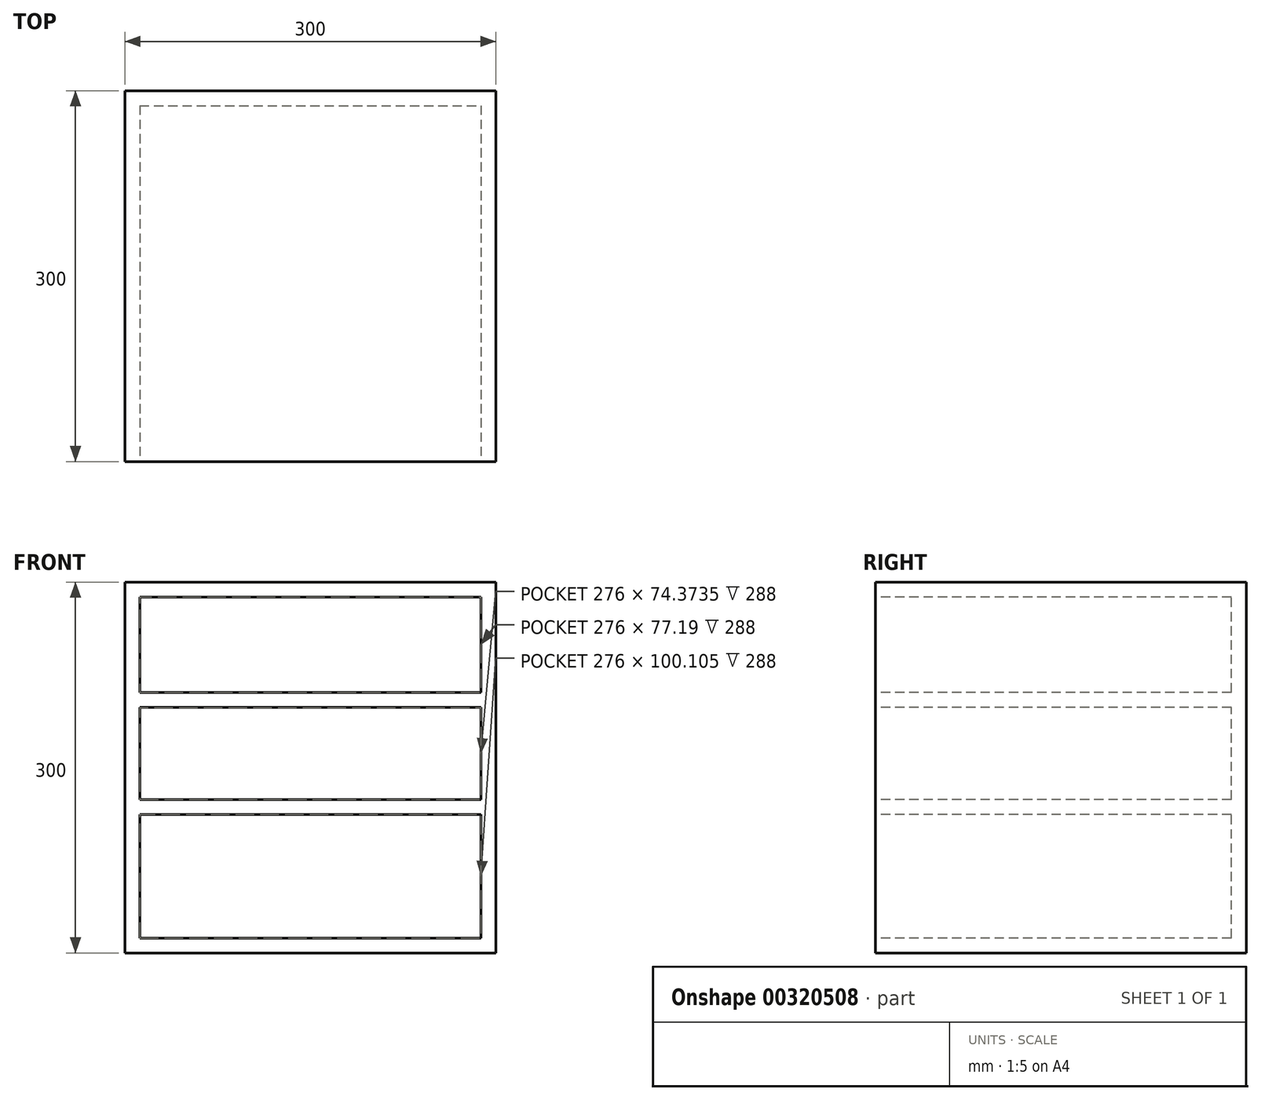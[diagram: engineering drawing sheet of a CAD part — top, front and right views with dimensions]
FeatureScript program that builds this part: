
annotation { "Feature Type Name" : "Feature", "Feature Type Description" : "" }
export const myFeature = defineFeature(function(context is Context, id is Id, definition is map)
    precondition{}
    {
        {
            var Q0;
            Q0=qCreatedBy(makeId("Front.planeOp"),FACE);
            var sketch = newSketch(context, id + "F0", { "sketchPlane" : qUnion([Q0])});
            skLineSegment(sketch, "E0.bottom", {"start": v(-150, -150) * mm, "end": v(150, -150) * mm});
            skLineSegment(sketch, "E0.top", {"start": v(-150, 150) * mm, "end": v(150, 150) * mm});
            skLineSegment(sketch, "E0.left", {"start": v(-150, -150) * mm, "end": v(-150, 150) * mm});
            skLineSegment(sketch, "E0.right", {"start": v(150, -150) * mm, "end": v(150, 150) * mm});
            skPoint(sketch, "E0.middle", {"position": v(0, 0) * mm});
            skSolve(sketch);
        }
        {
            var Q0;
            Q0=makeQuery(id+"F0.imprint","IMPRINT",FACE,{"disambiguationData":[TD([[makeQuery(id+"F0.imprint","IMPRINT",EDGE,{"derivedFrom":sQuery(id+"F0.wireOp",EDGE,"E0.bottom")}),1.0]])]});
            extrude(context, id + "F1", {"entities" : qUnion([Q0]), "oppositeDirection" : true, "depth" : 300 * mm});
        }
        {
            var Q0;
            Q0=makeQuery(id+"F1.opExtrude","CAP_FACE",FACE,{"disambiguationData":[OSD([sQuery(id+"F0.wireOp",EDGE,"E0.bottom"),sQuery(id+"F0.wireOp",EDGE,"E0.top"),sQuery(id+"F0.wireOp",EDGE,"E0.left"),sQuery(id+"F0.wireOp",EDGE,"E0.right")])],"isStart":true});
            shell(context, id + "F2", {"entities" : qUnion([Q0]), "thickness" : 12 * mm});
        }
        {
            var Q0;
            Q0=makeQuery(id+"F1.opExtrude","CAP_FACE",FACE,{"disambiguationData":[OSD([sQuery(id+"F0.wireOp",EDGE,"E0.bottom"),sQuery(id+"F0.wireOp",EDGE,"E0.top"),sQuery(id+"F0.wireOp",EDGE,"E0.left"),sQuery(id+"F0.wireOp",EDGE,"E0.right")])],"isStart":true});
            var sketch = newSketch(context, id + "F3", { "sketchPlane" : qUnion([Q0])});
            skLineSegment(sketch, "E1.bottom", {"start": v(-147.5, 48.48) * mm, "end": v(147.5, 48.48) * mm});
            skLineSegment(sketch, "E1.top", {"start": v(-147.5, 60.81) * mm, "end": v(147.5, 60.81) * mm});
            skLineSegment(sketch, "E1.left", {"start": v(-147.5, 48.48) * mm, "end": v(-147.5, 60.81) * mm});
            skLineSegment(sketch, "E1.right", {"start": v(147.5, 48.48) * mm, "end": v(147.5, 60.81) * mm});
            skPoint(sketch, "E1.middle", {"position": v(0, 54.64) * mm});
            skLineSegment(sketch, "E2.bottom", {"start": v(-147.5, -25.9) * mm, "end": v(147.5, -25.9) * mm});
            skLineSegment(sketch, "E2.top", {"start": v(-147.5, -37.9) * mm, "end": v(147.5, -37.9) * mm});
            skLineSegment(sketch, "E2.left", {"start": v(-147.5, -25.9) * mm, "end": v(-147.5, -37.9) * mm});
            skLineSegment(sketch, "E2.right", {"start": v(147.5, -25.9) * mm, "end": v(147.5, -37.9) * mm});
            skPoint(sketch, "E2.middle", {"position": v(0, -31.9) * mm});
            skSolve(sketch);
        }
        {
            var Q0;
            {var subQ0=sQuery(id+"F3.wireOp",EDGE,"E1.bottom");var subQ1=sQuery(id+"F0.wireOp",EDGE,"E0.left");var subQ2=makeQuery(id+"F2.opShell","OFFSET_EDGE",EDGE,{"disambiguationData":[OSD([subQ1]),TDD([makeQuery(id+"F1.opExtrude","CAP_EDGE",EDGE,{"disambiguationData":[OSD([subQ1])],"isStart":true})])]});var subQ3=makeQuery(id+"F3.imprint","INTERSECT",VERTEX,{"derivedFrom":[subQ2,subQ0]});Q0=makeQuery(id+"F3.imprint","IMPRINT",FACE,{"disambiguationData":[TD([[makeQuery(id+"F3.imprint","IMPRINT",EDGE,{"disambiguationData":[TD([[subQ3,-1.0]])],"derivedFrom":subQ0}),1.0]])]});}
            var Q1;
            {var subQ0=sQuery(id+"F3.wireOp",EDGE,"E2.bottom");var subQ1=sQuery(id+"F0.wireOp",EDGE,"E0.left");var subQ2=makeQuery(id+"F2.opShell","OFFSET_EDGE",EDGE,{"disambiguationData":[OSD([subQ1]),TDD([makeQuery(id+"F1.opExtrude","CAP_EDGE",EDGE,{"disambiguationData":[OSD([subQ1])],"isStart":true})])]});var subQ3=makeQuery(id+"F3.imprint","INTERSECT",VERTEX,{"derivedFrom":[subQ2,subQ0]});Q1=makeQuery(id+"F3.imprint","IMPRINT",FACE,{"disambiguationData":[TD([[makeQuery(id+"F3.imprint","IMPRINT",EDGE,{"disambiguationData":[TD([[subQ3,-1.0]])],"derivedFrom":subQ0}),-1.0]])]});}
            extrude(context, id + "F4", {"entities" : qUnion([Q0, Q1]), "operationType" : NewBodyOperationType.ADD, "oppositeDirection" : true, "depth" : 295 * mm});
        }
    });
